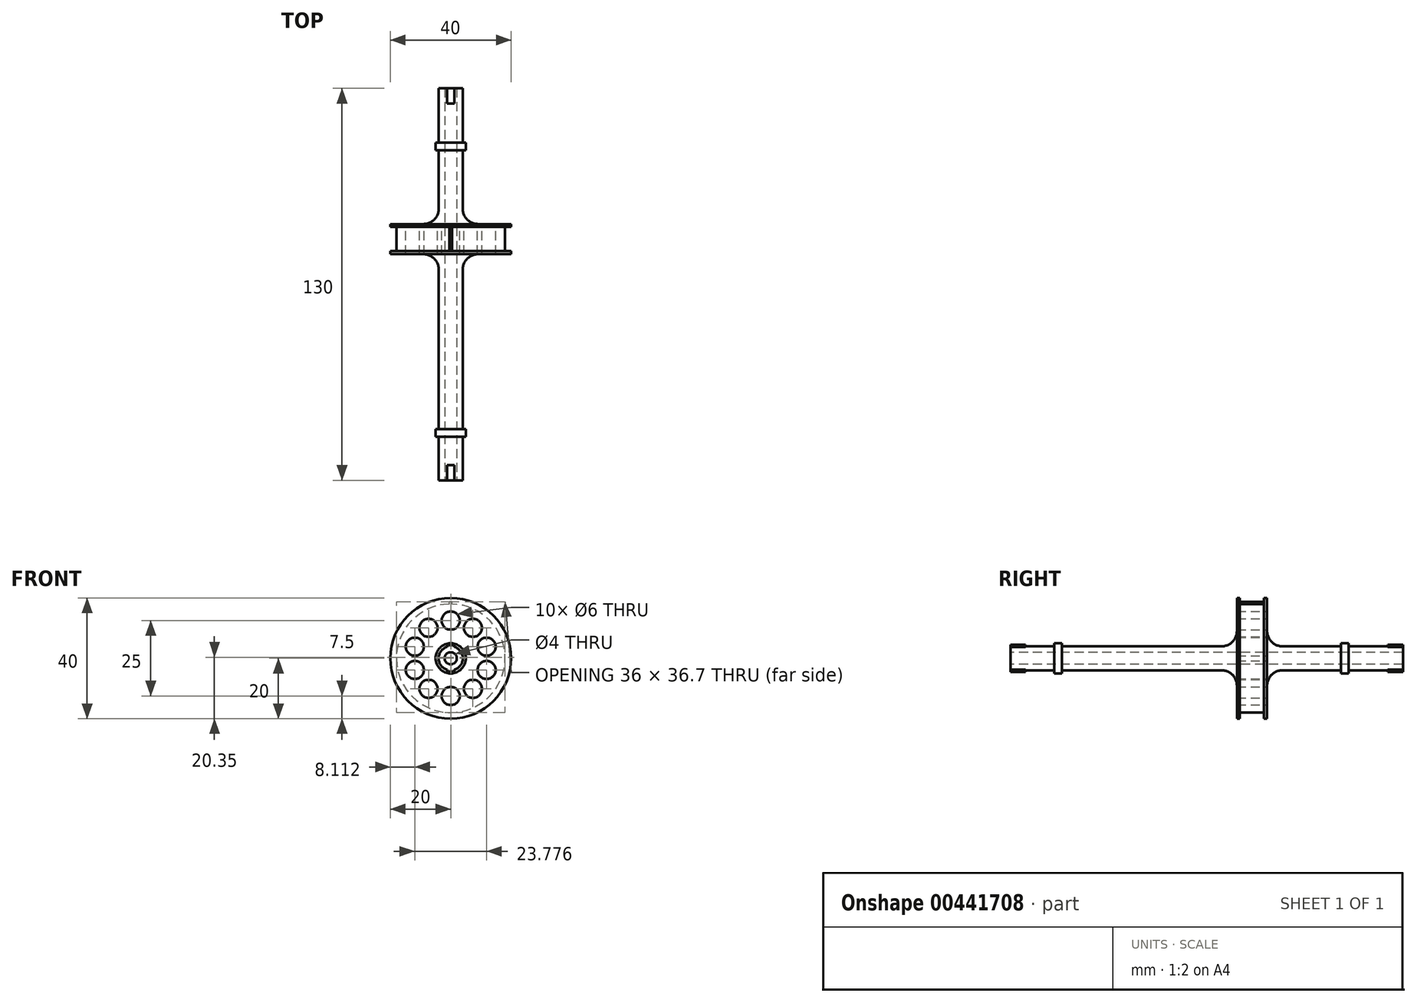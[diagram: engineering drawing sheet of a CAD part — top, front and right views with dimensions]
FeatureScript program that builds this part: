
annotation { "Feature Type Name" : "Feature", "Feature Type Description" : "" }
export const myFeature = defineFeature(function(context is Context, id is Id, definition is map)
    precondition{}
    {
        {
            var Q0;
            Q0=qCreatedBy(makeId("Front.planeOp"),FACE);
            var sketch = newSketch(context, id + "F0", { "sketchPlane" : qUnion([Q0])});
            skCircle(sketch, "E0", {"center": v(0, 0) * mm, "radius": 20 * mm});
            skSolve(sketch);
        }
        {
            var Q0;
            Q0 = qSketchRegion(id + "F0", true);
            extrude(context, id + "F1", {"entities" : qUnion([Q0]), "endBound" : BoundingType.SYMMETRIC, "depth" : 10 * mm});
        }
        {
            var Q0;
            Q0=qCreatedBy(makeId("Front.planeOp"),FACE);
            var sketch = newSketch(context, id + "F2", { "sketchPlane" : qUnion([Q0])});
            skCircle(sketch, "E1", {"center": v(0, 0) * mm, "radius": 4 * mm});
            skSolve(sketch);
        }
        {
            var Q0;
            Q0 = qSketchRegion(id + "F2", true);
            extrude(context, id + "F3", {"entities" : qUnion([Q0]), "operationType" : NewBodyOperationType.ADD, "oppositeDirection" : true, "depth" : 50 * mm, "hasSecondDirection" : true, "secondDirectionOppositeDirection" : false, "secondDirectionDepth" : 80 * mm, "offsetDistance" : 25 * mm});
        }
        {
            var Q0;
            Q0=makeQuery(id+"F3.opExtrude","CAP_FACE",FACE,{"disambiguationData":[OSD([sQuery(id+"F2.wireOp",EDGE,"E1")])],"isStart":true});
            var sketch = newSketch(context, id + "F4", { "sketchPlane" : qUnion([Q0])});
            skLineSegment(sketch, "E2", {"start": v(0, 2.9) * mm, "end": v(0, -3.7) * mm, "construction": true});
            skLineSegment(sketch, "E3", {"start": v(-4.06, 0) * mm, "end": v(5.62, 0) * mm, "construction": true});
            skLineSegment(sketch, "E4.bottom", {"start": v(-1.25, 4.5) * mm, "end": v(1.25, 4.5) * mm});
            skLineSegment(sketch, "E4.top", {"start": v(-1.25, -4.5) * mm, "end": v(1.25, -4.5) * mm});
            skLineSegment(sketch, "E4.left", {"start": v(-1.25, 4.5) * mm, "end": v(-1.25, -4.5) * mm});
            skLineSegment(sketch, "E4.right", {"start": v(1.25, 4.5) * mm, "end": v(1.25, -4.5) * mm});
            skSolve(sketch);
        }
        {
            var Q0;
            Q0 = qSketchRegion(id + "F4", true);
            extrude(context, id + "F5", {"entities" : qUnion([Q0]), "operationType" : NewBodyOperationType.ADD, "oppositeDirection" : true, "depth" : 5 * mm});
        }
        {
            var Q0;
            Q0=makeQuery(id+"F5.boolean.opBoolean","MERGE",FACE,{"derivedFrom":[makeQuery(id+"F3.opExtrude","CAP_FACE",FACE,{"disambiguationData":[OSD([sQuery(id+"F2.wireOp",EDGE,"E1")])],"isStart":true}),makeQuery(id+"F5.opExtrude","CAP_FACE",FACE,{"disambiguationData":[OSD([sQuery(id+"F4.wireOp",EDGE,"E4.bottom"),sQuery(id+"F4.wireOp",EDGE,"E4.top"),sQuery(id+"F4.wireOp",EDGE,"E4.left"),sQuery(id+"F4.wireOp",EDGE,"E4.right")])],"isStart":true})]});
            var sketch = newSketch(context, id + "F6", { "sketchPlane" : qUnion([Q0])});
            skCircle(sketch, "E5", {"center": v(0, 0) * mm, "radius": 2 * mm});
            skSolve(sketch);
        }
        {
            var Q0;
            Q0 = qSketchRegion(id + "F6", true);
            extrude(context, id + "F7", {"entities" : qUnion([Q0]), "operationType" : NewBodyOperationType.REMOVE, "endBound" : BoundingType.THROUGH_ALL, "oppositeDirection" : true, "depth" : 12 * mm});
        }
        {
            var Q0;
            Q0=qCreatedBy(makeId("Front.planeOp"),FACE);
            cPlane(context, id + "F8", {"entities" : qUnion([Q0]), "cplaneType" : CPlaneType.OFFSET, "offset" : 65.5 * mm, "width" : 150 * mm, "height" : 150 * mm});
        }
        {
            var Q0;
            Q0=qCreatedBy(id+"F8.planeOp",FACE);
            var sketch = newSketch(context, id + "F9", { "sketchPlane" : qUnion([Q0])});
            skCircle(sketch, "E6", {"center": v(0, 0) * mm, "radius": 5 * mm});
            skSolve(sketch);
        }
        {
            var Q0;
            Q0=makeQuery(id+"F9.imprint","IMPRINT",FACE,{"disambiguationData":[TD([[makeQuery(id+"F9.imprint","IMPRINT",EDGE,{"derivedFrom":sQuery(id+"F9.wireOp",EDGE,"E6")}),1.0]])]});
            extrude(context, id + "F10", {"entities" : qUnion([Q0]), "operationType" : NewBodyOperationType.ADD, "oppositeDirection" : true, "depth" : 2.5 * mm});
        }
        {
            var Q0;
            Q0=qCreatedBy(makeId("Front.planeOp"),FACE);
            cPlane(context, id + "F11", {"entities" : qUnion([Q0]), "cplaneType" : CPlaneType.OFFSET, "offset" : 32 * mm, "oppositeDirection" : true, "width" : 150 * mm, "height" : 150 * mm});
        }
        {
            var Q0;
            Q0=qCreatedBy(id+"F11.planeOp",FACE);
            var sketch = newSketch(context, id + "F12", { "sketchPlane" : qUnion([Q0])});
            skCircle(sketch, "E7", {"center": v(0, 0) * mm, "radius": 5 * mm});
            skSolve(sketch);
        }
        {
            var Q0;
            Q0 = qSketchRegion(id + "F12", true);
            extrude(context, id + "F13", {"entities" : qUnion([Q0]), "operationType" : NewBodyOperationType.ADD, "depth" : 2.5 * mm});
        }
        {
            var Q0;
            Q0=makeQuery(id+"F3.opExtrude","CAP_FACE",FACE,{"disambiguationData":[OSD([sQuery(id+"F2.wireOp",EDGE,"E1")])],"isStart":false});
            var sketch = newSketch(context, id + "F14", { "sketchPlane" : qUnion([Q0])});
            skLineSegment(sketch, "E8.bottom", {"start": v(-1.25, 4.5) * mm, "end": v(1.25, 4.5) * mm});
            skLineSegment(sketch, "E8.top", {"start": v(-1.25, -4.5) * mm, "end": v(1.25, -4.5) * mm});
            skLineSegment(sketch, "E8.left", {"start": v(-1.25, 4.5) * mm, "end": v(-1.25, -4.5) * mm});
            skLineSegment(sketch, "E8.right", {"start": v(1.25, 4.5) * mm, "end": v(1.25, -4.5) * mm});
            skLineSegment(sketch, "E9", {"start": v(0, 4.6) * mm, "end": v(0, -4.66) * mm, "construction": true});
            skPoint(sketch, "E9.endSnap0", {"position": v(0, -4.5) * mm});
            skLineSegment(sketch, "E10", {"start": v(-5.04, 0) * mm, "end": v(5.8, 0) * mm, "construction": true});
            skSolve(sketch);
        }
        {
            var Q0;
            Q0 = qSketchRegion(id + "F14", true);
            extrude(context, id + "F15", {"entities" : qUnion([Q0]), "operationType" : NewBodyOperationType.ADD, "oppositeDirection" : true, "depth" : 5 * mm});
        }
        {
            var Q0;
            Q0=makeQuery(id+"F15.boolean.opBoolean","MERGE",FACE,{"derivedFrom":[makeQuery(id+"F3.opExtrude","CAP_FACE",FACE,{"disambiguationData":[OSD([sQuery(id+"F2.wireOp",EDGE,"E1")])],"isStart":false}),makeQuery(id+"F15.opExtrude","CAP_FACE",FACE,{"disambiguationData":[OSD([sQuery(id+"F14.wireOp",EDGE,"E8.bottom"),sQuery(id+"F14.wireOp",EDGE,"E8.top"),sQuery(id+"F14.wireOp",EDGE,"E8.left"),sQuery(id+"F14.wireOp",EDGE,"E8.right")])],"isStart":true})]});
            var sketch = newSketch(context, id + "F16", { "sketchPlane" : qUnion([Q0])});
            skCircle(sketch, "E11", {"center": v(0, 0) * mm, "radius": 2 * mm});
            skSolve(sketch);
        }
        {
            var Q0;
            Q0 = qSketchRegion(id + "F16", true);
            extrude(context, id + "F17", {"entities" : qUnion([Q0]), "operationType" : NewBodyOperationType.REMOVE, "endBound" : BoundingType.THROUGH_ALL, "oppositeDirection" : true, "depth" : 25 * mm});
        }
        {
            var Q0;
            Q0=makeQuery(id+"F3.boolean.opBoolean","INTERSECT",EDGE,{"derivedFrom":[makeQuery(id+"F1.opExtrude","CAP_FACE",FACE,{"disambiguationData":[OSD([sQuery(id+"F0.wireOp",EDGE,"E0")])],"isStart":false}),makeQuery(id+"F3.opExtrude","SWEPT_FACE",FACE,{"disambiguationData":[OSD([sQuery(id+"F2.wireOp",EDGE,"E1")])]})]});
            var Q1;
            Q1=makeQuery(id+"F3.boolean.opBoolean","INTERSECT",EDGE,{"derivedFrom":[makeQuery(id+"F1.opExtrude","CAP_FACE",FACE,{"disambiguationData":[OSD([sQuery(id+"F0.wireOp",EDGE,"E0")])],"isStart":true}),makeQuery(id+"F3.opExtrude","SWEPT_FACE",FACE,{"disambiguationData":[OSD([sQuery(id+"F2.wireOp",EDGE,"E1")])]})]});
            fillet(context, id + "F18", {"entities" : qUnion([Q0, Q1]), "radius" : 5 * mm, "tangentPropagation" : true, "allowEdgeOverflow" : false});
        }
        {
            var Q0;
            Q0=qCreatedBy(makeId("Right.planeOp"),FACE);
            var sketch = newSketch(context, id + "F19", { "sketchPlane" : qUnion([Q0])});
            skLineSegment(sketch, "E12", {"start": v(-8.12, 20) * mm, "end": v(8.92, 20) * mm, "construction": true});
            skLineSegment(sketch, "E13", {"start": v(-81.56, 0) * mm, "end": v(62.38, 0) * mm, "construction": true});
            skLineSegment(sketch, "E14", {"start": v(-4, 20) * mm, "end": v(-4, 18) * mm});
            skLineSegment(sketch, "E15", {"start": v(-4, 18) * mm, "end": v(4, 18) * mm});
            skLineSegment(sketch, "E16", {"start": v(4, 18) * mm, "end": v(4, 20) * mm});
            skLineSegment(sketch, "E17", {"start": v(4, 20) * mm, "end": v(5, 20) * mm});
            skLineSegment(sketch, "E18", {"start": v(-4, 20) * mm, "end": v(-5, 20) * mm});
            skLineSegment(sketch, "E19", {"start": v(0, 20.6) * mm, "end": v(0, 16.47) * mm, "construction": true});
            skLineSegment(sketch, "E20", {"start": v(-4, 20) * mm, "end": v(4, 20) * mm});
            skSolve(sketch);
        }
        {
            var Q0;
            Q0 = qSketchRegion(id + "F19", true);
            var Q1;
            Q1=makeQuery(id+"F1.opExtrude","CAP_EDGE",EDGE,{"disambiguationData":[OSD([sQuery(id+"F0.wireOp",EDGE,"E0")])],"isStart":false});
            sweep(context, id + "F20", {"operationType" : NewBodyOperationType.REMOVE, "profiles" : qUnion([Q0]), "path" : qUnion([Q1])});
        }
        {
            var Q0;
            Q0=qCreatedBy(makeId("Right.planeOp"),FACE);
            var sketch = newSketch(context, id + "F21", { "sketchPlane" : qUnion([Q0])});
            skLineSegment(sketch, "E21", {"start": v(-4, 18.7) * mm, "end": v(-4, 13.7) * mm});
            skLineSegment(sketch, "E22", {"start": v(-4, 13.7) * mm, "end": v(4, 13.7) * mm});
            skLineSegment(sketch, "E23", {"start": v(4, 13.7) * mm, "end": v(4, 18.7) * mm});
            skLineSegment(sketch, "E24", {"start": v(4, 18.7) * mm, "end": v(-4, 18.7) * mm});
            skLineSegment(sketch, "E25", {"start": v(0, 24.1) * mm, "end": v(0, 9.8) * mm, "construction": true});
            skLineSegment(sketch, "E26", {"start": v(-4, 18) * mm, "end": v(4, 18) * mm});
            skLineSegment(sketch, "E27", {"start": v(-81.8, 0) * mm, "end": v(59.85, 0) * mm, "construction": true});
            skSolve(sketch);
        }
        {
            var Q0;
            Q0 = qSketchRegion(id + "F21", true);
            extrude(context, id + "F22", {"entities" : qUnion([Q0]), "operationType" : NewBodyOperationType.ADD, "endBound" : BoundingType.SYMMETRIC, "depth" : 1 * mm, "offsetDistance" : 25 * mm});
        }
        {
            var Q0;
            Q0=makeQuery(id+"F1.opExtrude","CAP_FACE",FACE,{"disambiguationData":[OSD([sQuery(id+"F0.wireOp",EDGE,"E0")])],"isStart":true});
            var sketch = newSketch(context, id + "F23", { "sketchPlane" : qUnion([Q0])});
            skLineSegment(sketch, "E28", {"start": v(0, 16.4) * mm, "end": v(0, -16.94) * mm, "construction": true});
            skCircle(sketch, "E29", {"center": v(0, 12.5) * mm, "radius": 3 * mm});
            skCircle(sketch, "E30.1.0", {"center": v(-7.35, 10.11) * mm, "radius": 3 * mm});
            skCircle(sketch, "E30.2.0", {"center": v(-11.89, 3.86) * mm, "radius": 3 * mm});
            skCircle(sketch, "E30.3.0", {"center": v(-11.89, -3.86) * mm, "radius": 3 * mm});
            skCircle(sketch, "E30.4.0", {"center": v(-7.35, -10.11) * mm, "radius": 3 * mm});
            skCircle(sketch, "E30.5.0", {"center": v(0, -12.5) * mm, "radius": 3 * mm});
            skCircle(sketch, "E30.6.0", {"center": v(7.35, -10.11) * mm, "radius": 3 * mm});
            skCircle(sketch, "E30.7.0", {"center": v(11.89, -3.86) * mm, "radius": 3 * mm});
            skCircle(sketch, "E30.8.0", {"center": v(11.89, 3.86) * mm, "radius": 3 * mm});
            skCircle(sketch, "E30.9.0", {"center": v(7.35, 10.11) * mm, "radius": 3 * mm});
            skPoint(sketch, "E30.center", {"position": v(0, 0) * mm});
            skSolve(sketch);
        }
        {
            var Q0;
            Q0 = qSketchRegion(id + "F23", true);
            extrude(context, id + "F24", {"entities" : qUnion([Q0]), "operationType" : NewBodyOperationType.REMOVE, "endBound" : BoundingType.THROUGH_ALL, "oppositeDirection" : true, "depth" : 25 * mm});
        }
    });
